# Revit family: JCI_Tyco_Union_Grv_One_Bolt_Coup_8_(DN200)
name_source: partatom
category: Pipe Fittings
units: mm (PartAtom-declared; Revit-internal decimal feet)

## family parameters
Always vertical = Yes
Cut with Voids When Loaded = No
OmniClass Number = 23.60.30.11.14
OmniClass Title = Pipework Fittings
Part Type = Union
Round Connector Dimension = Use Diameter
Shared = No
Work Plane-Based = No

## types (3) — shared parameters
COBie = Yes
COBie.Type = Yes
Description = JCI_Tyco_Union_Grv_One_Bolt_Coup_8_(DN200)
Manufacturer = Tyco Fire Protection Products
Manufacturer URL = www.tyco-fire.com
Material_ = Ductile Iron
Model = Grv One-Bolt Coup 8 (DN200)
Technical Data Sheet No = TFP1856
zero-valued in all types: COBie.Type.NominalHeight, COBie.Type.NominalLength, COBie.Type.NominalWidth, COBie.Type.ReplacementCost, Default Elevation

## per-type parameters (varying)
| type | COBie.Type.AssetType | COBie.Type.Category | COBie.Type.DurationUnit | COBie.Type.Manufacturer | COBie.Type.Material | COBie.Type.ModelNumber | COBie.Type.ModelReference | COBie.Type.Size | COBie.Type.WarrantyDurationParts | COBie.Type.WarrantyDurationUnit | Finish_ |
| JCI_Tyco_Union_Grv_One_Bolt_Coup_8_(DN200) DI/Galv |  |  |  |  |  |  |  |  |  |  | Galvanized |
| JCI_Tyco_Union_Grv_One_Bolt_Coup_8_(DN200) DI/Orng |  |  |  |  |  |  |  |  |  |  | Orange |
| JCI_Tyco_Union_Grv_One_Bolt_Coup_8_(DN200) DI/Red3000 | Fixed | Pr_65_52_63_11:Fittings | year | Tyco Fire Protection Products | Ductile Iron | 579-11-R | G-FIRE Fig.579 Grooved One-Bolt Rigid Coupling 8" (DN200) Red | 8 x 8 | 10 | year | Red |

## geometry (parser evidence)
native form markers: Sweep x56
no freeform markers — native parametric forms only
